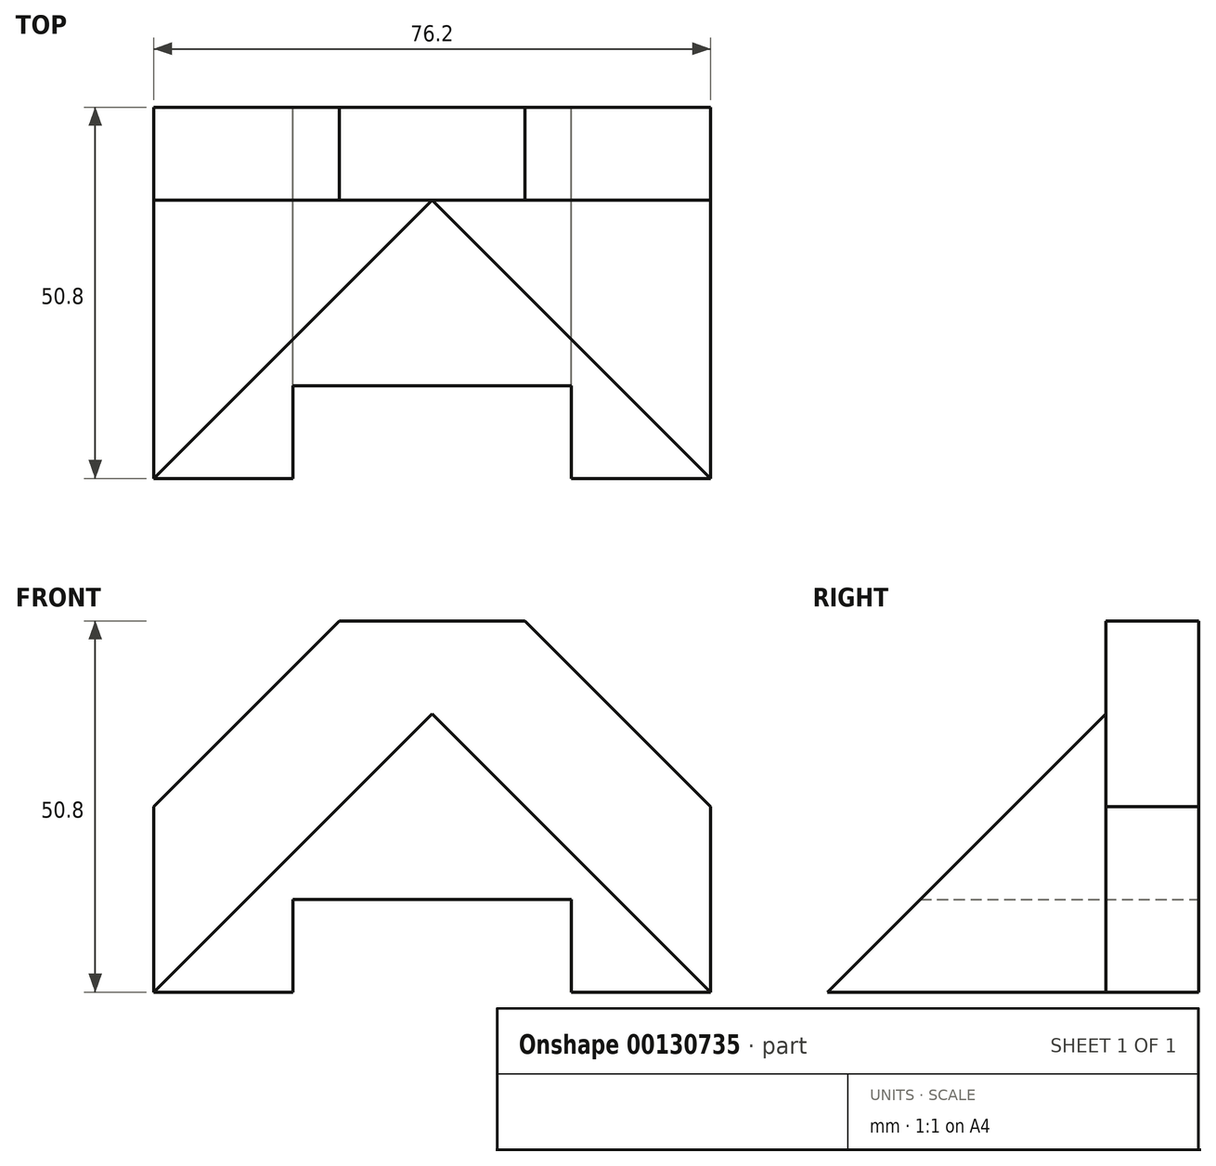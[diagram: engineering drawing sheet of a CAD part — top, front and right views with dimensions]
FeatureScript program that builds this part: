
annotation { "Feature Type Name" : "Feature", "Feature Type Description" : "" }
export const myFeature = defineFeature(function(context is Context, id is Id, definition is map)
    precondition{}
    {
        {
            var Q0;
            Q0=qCreatedBy(makeId("Front.planeOp"),FACE);
            var sketch = newSketch(context, id + "F0", { "sketchPlane" : qUnion([Q0])});
            skLineSegment(sketch, "E0", {"start": v(0, 0) * mm, "end": v(0, 25.4) * mm});
            skLineSegment(sketch, "E1", {"start": v(0, 25.4) * mm, "end": v(25.4, 50.8) * mm});
            skLineSegment(sketch, "E2", {"start": v(25.4, 50.8) * mm, "end": v(50.8, 50.8) * mm});
            skLineSegment(sketch, "E3", {"start": v(50.8, 50.8) * mm, "end": v(76.2, 25.4) * mm});
            skLineSegment(sketch, "E4", {"start": v(76.2, 25.4) * mm, "end": v(76.2, 0) * mm});
            skLineSegment(sketch, "E5", {"start": v(76.2, 0) * mm, "end": v(0, 0) * mm});
            skLineSegment(sketch, "E6", {"start": v(0, 0) * mm, "end": v(38.1, 38.1) * mm});
            skLineSegment(sketch, "E7", {"start": v(38.1, 38.1) * mm, "end": v(76.2, 0) * mm});
            skLineSegment(sketch, "E8.bottom", {"start": v(19.05, 0) * mm, "end": v(57.15, 0) * mm});
            skLineSegment(sketch, "E8.top", {"start": v(19.05, 12.7) * mm, "end": v(57.15, 12.7) * mm});
            skLineSegment(sketch, "E8.left", {"start": v(19.05, 0) * mm, "end": v(19.05, 12.7) * mm});
            skLineSegment(sketch, "E8.right", {"start": v(57.15, 0) * mm, "end": v(57.15, 12.7) * mm});
            skSolve(sketch);
        }
        {
            var Q0;
            {var subQ1=sQuery(id+"F0.wireOp",EDGE,"E6");Q0=makeQuery(id+"F0.imprint","IMPRINT",FACE,{"disambiguationData":[TD([[makeQuery(id+"F0.imprint","IMPRINT",EDGE,{"derivedFrom":subQ1}),-1.0]])]});}
            var Q1;
            Q1=makeQuery(id+"F0.imprint","IMPRINT",FACE,{"disambiguationData":[TD([[makeQuery(id+"F0.imprint","IMPRINT",EDGE,{"derivedFrom":sQuery(id+"F0.wireOp",EDGE,"E8.bottom")}),1.0]])]});
            extrude(context, id + "F1", {"entities" : qUnion([Q0, Q1]), "depth" : 50.8 * mm});
        }
        {
            var Q0;
            Q0=makeQuery(id+"F1.opExtrude","CAP_FACE",FACE,{"disambiguationData":[OSD([sQuery(id+"F0.wireOp",EDGE,"E5"),sQuery(id+"F0.wireOp",EDGE,"E6"),sQuery(id+"F0.wireOp",EDGE,"E7"),sQuery(id+"F0.wireOp",EDGE,"E8.bottom")])],"isStart":false});
            var sketch = newSketch(context, id + "F2", { "sketchPlane" : qUnion([Q0])});
            skLineSegment(sketch, "E9.bottom", {"start": v(19.05, 0) * mm, "end": v(57.15, 0) * mm});
            skLineSegment(sketch, "E9.top", {"start": v(19.05, 12.7) * mm, "end": v(57.15, 12.7) * mm});
            skLineSegment(sketch, "E9.left", {"start": v(19.05, 0) * mm, "end": v(19.05, 12.7) * mm});
            skLineSegment(sketch, "E9.right", {"start": v(57.15, 0) * mm, "end": v(57.15, 12.7) * mm});
            skSolve(sketch);
        }
        {
            var Q0;
            Q0 = qSketchRegion(id + "F2", true);
            extrude(context, id + "F3", {"entities" : qUnion([Q0]), "operationType" : NewBodyOperationType.REMOVE, "oppositeDirection" : true, "depth" : 12.7 * mm});
        }
        {
            var Q0;
            Q0=makeQuery(id+"F0.imprint","IMPRINT",FACE,{"disambiguationData":[TD([[makeQuery(id+"F0.imprint","IMPRINT",EDGE,{"derivedFrom":sQuery(id+"F0.wireOp",EDGE,"E0")}),-1.0]])]});
            extrude(context, id + "F4", {"entities" : qUnion([Q0]), "operationType" : NewBodyOperationType.ADD, "depth" : 12.7 * mm});
        }
        {
            var Q0;
            Q0=qCreatedBy(makeId("Right.planeOp"),FACE);
            var sketch = newSketch(context, id + "F5", { "sketchPlane" : qUnion([Q0])});
            skLineSegment(sketch, "E10", {"start": v(-50.8, 0) * mm, "end": v(-12.7, 38.1) * mm});
            skLineSegment(sketch, "E11", {"start": v(-12.7, 38.1) * mm, "end": v(-50.8, 38.1) * mm});
            skLineSegment(sketch, "E12", {"start": v(-50.8, 38.1) * mm, "end": v(-50.8, 0) * mm});
            skSolve(sketch);
        }
        {
            var Q0;
            Q0 = qSketchRegion(id + "F5", true);
            extrude(context, id + "F6", {"entities" : qUnion([Q0]), "operationType" : NewBodyOperationType.REMOVE, "endBound" : BoundingType.THROUGH_ALL, "depth" : 25.4 * mm});
        }
    });
